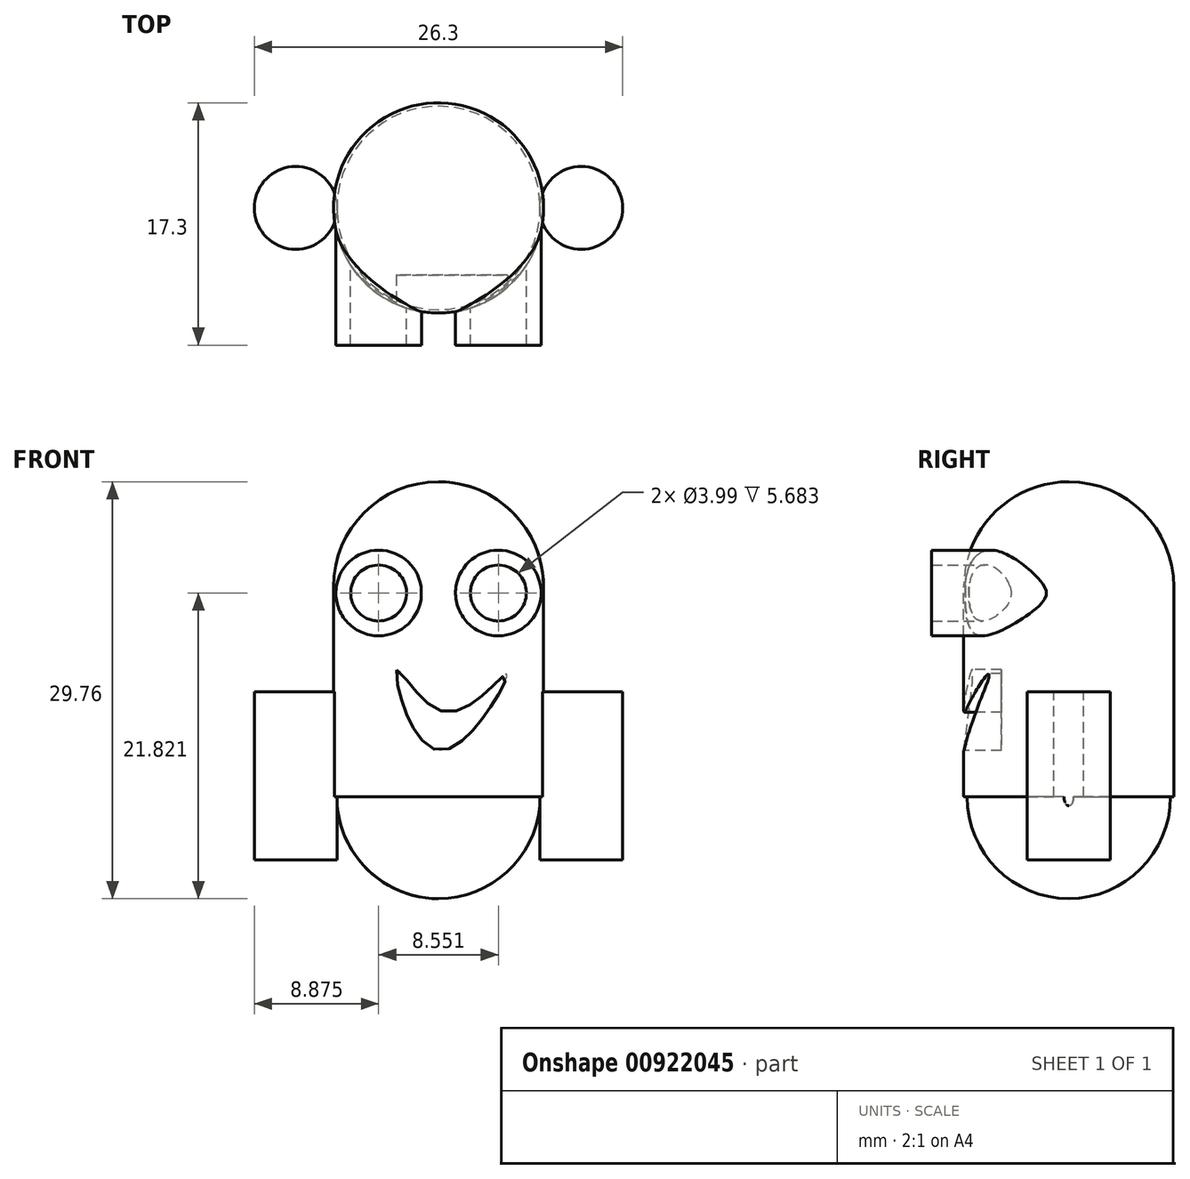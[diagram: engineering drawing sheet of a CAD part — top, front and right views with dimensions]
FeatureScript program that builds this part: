
annotation { "Feature Type Name" : "Feature", "Feature Type Description" : "" }
export const myFeature = defineFeature(function(context is Context, id is Id, definition is map)
    precondition{}
    {
        {
            var Q0;
            Q0=qCreatedBy(makeId("Front.planeOp"),FACE);
            var sketch = newSketch(context, id + "F0", { "sketchPlane" : qUnion([Q0])});
            skLineSegment(sketch, "E0.bottom", {"start": v(7.5, -7.5) * mm, "end": v(7.26, -7.5) * mm});
            skLineSegment(sketch, "E0.right", {"start": v(-7.5, -7.5) * mm, "end": v(-7.5, 7.5) * mm});
            skPoint(sketch, "E0.middle", {"position": v(0, 0) * mm});
            skArc(sketch, "E1", {"start": v(0, 15) * mm, "mid": v(-5.3, 12.8) * mm, "end": v(-7.5, 7.5) * mm});
            skArc(sketch, "E2", {"start": v(-7.26, -7.5) * mm, "mid": v(-5.13, -12.63) * mm, "end": v(0, -14.76) * mm});
            skLineSegment(sketch, "E3", {"start": v(0, 15) * mm, "end": v(0, -14.76) * mm});
            skPoint(sketch, "E0.left.end.orphan", {"position": v(7.5, 7.5) * mm});
            skLineSegment(sketch, "E4.trimOffspring", {"start": v(-7.26, -7.5) * mm, "end": v(-7.5, -7.5) * mm});
            skSolve(sketch);
        }
        {
            var Q0;
            Q0=makeQuery(id+"F0.imprint","IMPRINT",FACE,{"disambiguationData":[TD([[makeQuery(id+"F0.imprint","IMPRINT",EDGE,{"derivedFrom":sQuery(id+"F0.wireOp",EDGE,"E0.right")}),-1.0]])]});
            var Q1;
            Q1=sQuery(id+"F0.wireOp",EDGE,"E3");
            revolve(context, id + "F1", {"surfaceOperationType" : NewSurfaceOperationType.NEW, "entities" : qUnion([Q0]), "axis" : qUnion([Q1]), "revolveType" : RevolveType.FULL});
        }
        {
            var Q0;
            Q0=qCreatedBy(makeId("Front.planeOp"),FACE);
            var sketch = newSketch(context, id + "F2", { "sketchPlane" : qUnion([Q0])});
            skLineSegment(sketch, "E5", {"start": v(0, 13.29) * mm, "end": v(0, -9.21) * mm, "construction": true});
            skCircle(sketch, "E6", {"center": v(-4.28, 7.06) * mm, "radius": 3.06 * mm});
            skCircle(sketch, "E7", {"center": v(-4.28, 7.06) * mm, "radius": 2 * mm});
            skCircle(sketch, "E8.MirrorC", {"center": v(4.28, 7.06) * mm, "radius": 3.06 * mm});
            skCircle(sketch, "E9.MirrorC", {"center": v(4.28, 7.06) * mm, "radius": 2 * mm});
            skSolve(sketch);
        }
        {
            var Q0;
            Q0 = qSketchRegion(id + "F2", true);
            extrude(context, id + "F3", {"entities" : qUnion([Q0]), "operationType" : NewBodyOperationType.ADD, "depth" : 9.8 * mm, "offsetDistance" : 25 * mm});
        }
        {
            var Q0;
            Q0=makeQuery(id+"F3.opExtrude","CAP_FACE",FACE,{"disambiguationData":[OSD([sQuery(id+"F2.wireOp",EDGE,"E6"),sQuery(id+"F2.wireOp",EDGE,"E7")])],"isStart":false});
            var sketch = newSketch(context, id + "F4", { "sketchPlane" : qUnion([Q0])});
            skFitSpline(sketch, "E10", {"points": [v(-2.97, 1.57) * mm, v(0, -4.19) * mm, v(4.91, 1.3) * mm, v(0.6, -1.44) * mm, v(-2.97, 1.57) * mm]});
            skSolve(sketch);
        }
        {
            var Q0;
            Q0 = qSketchRegion(id + "F4", true);
            extrude(context, id + "F5", {"entities" : qUnion([Q0]), "operationType" : NewBodyOperationType.REMOVE, "oppositeDirection" : true, "depth" : 5 * mm, "offsetDistance" : 25 * mm});
        }
        {
            var Q0;
            Q0=qCreatedBy(makeId("Top.planeOp"),FACE);
            var sketch = newSketch(context, id + "F6", { "sketchPlane" : qUnion([Q0])});
            skCircle(sketch, "E11", {"center": v(-10.2, 0) * mm, "radius": 2.96 * mm});
            skLineSegment(sketch, "E12", {"start": v(0, 5.74) * mm, "end": v(0, -3.08) * mm, "construction": true});
            skCircle(sketch, "E13.MirrorC", {"center": v(10.2, 0) * mm, "radius": 2.96 * mm});
            skSolve(sketch);
        }
        {
            var Q0;
            Q0 = qSketchRegion(id + "F6", true);
            extrude(context, id + "F7", {"entities" : qUnion([Q0]), "operationType" : NewBodyOperationType.ADD, "oppositeDirection" : true, "depth" : 12 * mm, "offsetDistance" : 25 * mm});
        }
    });
